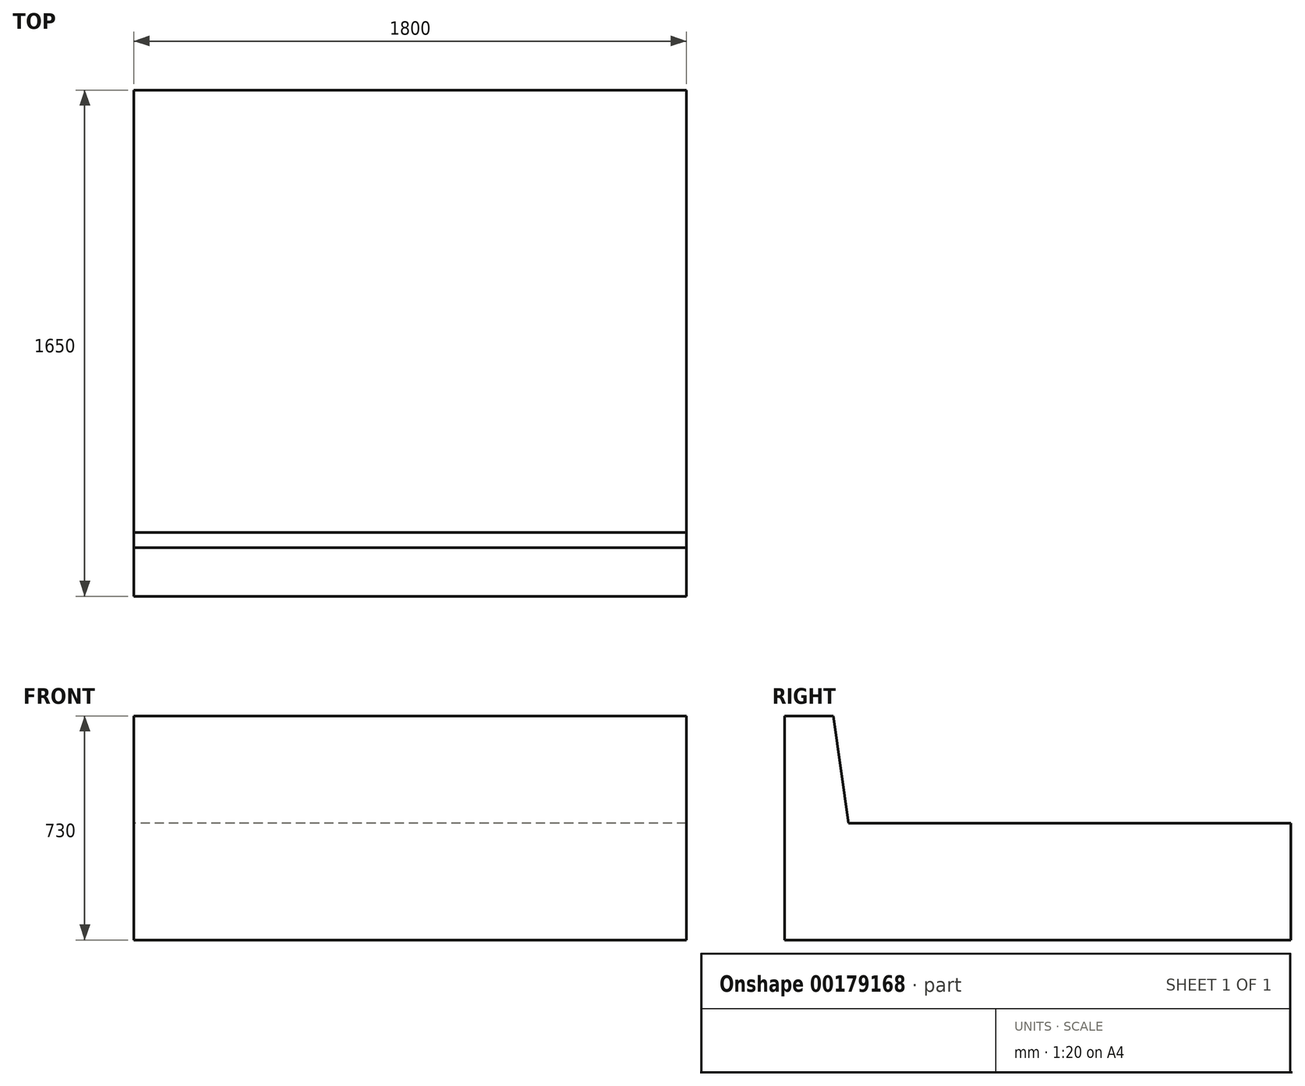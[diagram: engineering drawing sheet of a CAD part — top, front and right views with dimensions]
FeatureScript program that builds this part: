
annotation { "Feature Type Name" : "Feature", "Feature Type Description" : "" }
export const myFeature = defineFeature(function(context is Context, id is Id, definition is map)
    precondition{}
    {
        {
            var Q0;
            Q0=qCreatedBy(makeId("Right.planeOp"),FACE);
            var sketch = newSketch(context, id + "F0", { "sketchPlane" : qUnion([Q0])});
            skLineSegment(sketch, "E0", {"start": v(0, 0) * mm, "end": v(1650, 0) * mm});
            skLineSegment(sketch, "E1", {"start": v(0, 0) * mm, "end": v(0, 730) * mm});
            skLineSegment(sketch, "E2", {"start": v(0, 730) * mm, "end": v(158.64, 730) * mm});
            skLineSegment(sketch, "E3", {"start": v(158.64, 730) * mm, "end": v(208.37, 380) * mm});
            skLineSegment(sketch, "E4", {"start": v(208.37, 380) * mm, "end": v(1650, 380) * mm});
            skLineSegment(sketch, "E5", {"start": v(1650, 380) * mm, "end": v(1650, 0) * mm});
            skSolve(sketch);
        }
        {
            var Q0;
            Q0 = qSketchRegion(id + "F0", true);
            extrude(context, id + "F1", {"entities" : qUnion([Q0]), "depth" : 1800 * mm});
        }
    });
